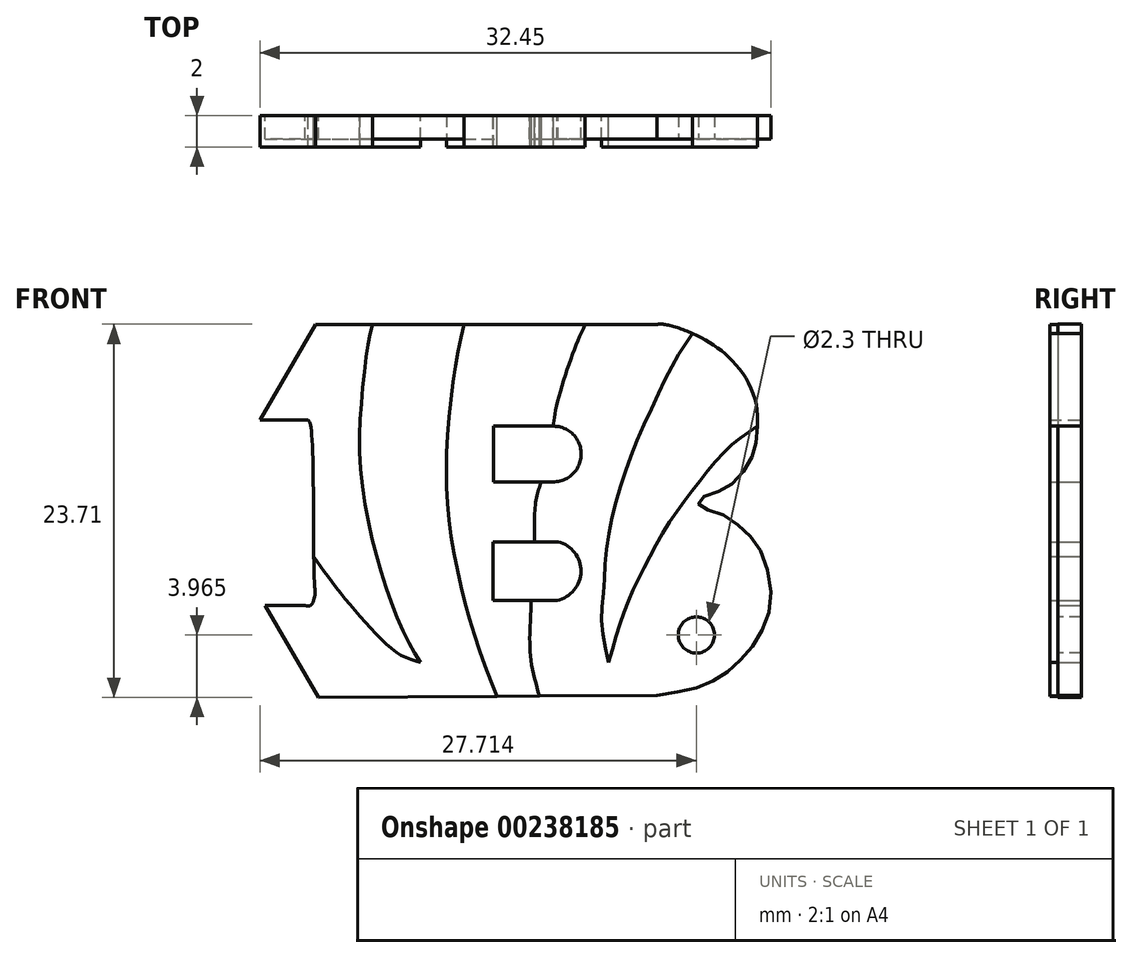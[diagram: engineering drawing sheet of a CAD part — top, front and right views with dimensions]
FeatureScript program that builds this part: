
annotation { "Feature Type Name" : "Feature", "Feature Type Description" : "" }
export const myFeature = defineFeature(function(context is Context, id is Id, definition is map)
    precondition{}
    {
        {
            var Q0;
            Q0=qCreatedBy(makeId("Front.planeOp"),FACE);
            var sketch = newSketch(context, id + "F0", { "sketchPlane" : qUnion([Q0])});
            skLineSegment(sketch, "E0", {"start": v(22.53, 20.5) * mm, "end": v(22.53, 16.97) * mm});
            skLineSegment(sketch, "E1", {"start": v(22.53, 16.97) * mm, "end": v(26.3, 16.97) * mm});
            skLineSegment(sketch, "E2", {"start": v(22.53, 20.5) * mm, "end": v(26.34, 20.5) * mm});
            skArc(sketch, "E3", {"start": v(26.3, 16.97) * mm, "mid": v(28.1, 18.71) * mm, "end": v(26.34, 20.5) * mm});
            skLineSegment(sketch, "E4", {"start": v(22.5, 13.16) * mm, "end": v(22.5, 9.43) * mm});
            skLineSegment(sketch, "E5", {"start": v(22.5, 9.43) * mm, "end": v(26.57, 9.43) * mm});
            skLineSegment(sketch, "E6", {"start": v(22.5, 13.16) * mm, "end": v(26.64, 13.16) * mm});
            skArc(sketch, "E7", {"start": v(26.57, 9.43) * mm, "mid": v(28.1, 11.27) * mm, "end": v(26.64, 13.16) * mm});
            skLineSegment(sketch, "E8", {"start": v(7.71, 20.9) * mm, "end": v(11.24, 26.96) * mm});
            skLineSegment(sketch, "E9", {"start": v(11.24, 26.96) * mm, "end": v(32.9, 26.96) * mm});
            skFitSpline(sketch, "E10", {"points": [v(32.9, 26.96) * mm, v(33.42, 26.96) * mm, v(34.85, 26.53) * mm, v(36.5, 25.65) * mm, v(38.05, 24.27) * mm, v(39.2, 21.97) * mm, v(39.24, 19.75) * mm, v(38.93, 18.48) * mm, v(37.9, 17.02) * mm, v(36.63, 16.27) * mm, v(35.6, 15.83) * mm, v(35.68, 15.4) * mm, v(36.83, 15) * mm, v(38.37, 13.97) * mm, v(39.48, 12.62) * mm, v(40.15, 9.93) * mm, v(39.64, 7.6) * mm, v(38.45, 5.89) * mm, v(37.06, 4.66) * mm, v(35.36, 3.87) * mm, v(32.9, 3.4) * mm], "startDerivative": vector(16.4, 1.57) * mm, "endDerivative": vector(-42.3, -6.3) * mm});
            skLineSegment(sketch, "E11", {"start": v(7.71, 20.9) * mm, "end": v(10.76, 20.9) * mm});
            skLineSegment(sketch, "E12", {"start": v(11.44, 3.27) * mm, "end": v(32.9, 3.4) * mm});
            skLineSegment(sketch, "E13", {"start": v(11.44, 3.27) * mm, "end": v(8.03, 9.1) * mm});
            skLineSegment(sketch, "E14", {"start": v(8.03, 9.1) * mm, "end": v(10.57, 9.11) * mm});
            skFitSpline(sketch, "E15", {"points": [v(10.57, 9.11) * mm, v(10.92, 9.11) * mm, v(11.2, 9.77) * mm, v(11.16, 10.68) * mm, v(10.96, 20.27) * mm, v(10.76, 20.9) * mm], "startDerivative": vector(4, -1.18) * mm, "endDerivative": vector(-1.7, 2.44) * mm});
            skFitSpline(sketch, "E16", {"points": [v(14.84, 26.96) * mm, v(14.53, 25.42) * mm, v(14.17, 22.25) * mm, v(14.05, 18.56) * mm, v(14.65, 14.17) * mm, v(15.71, 10.29) * mm, v(16.94, 7.16) * mm, v(17.9, 5.5) * mm], "startDerivative": vector(-3.2, -13.7) * mm, "endDerivative": vector(8.42, -13.46) * mm});
            skFitSpline(sketch, "E17", {"points": [v(11.12, 12.23) * mm, v(12.43, 10.4) * mm, v(14.49, 7.95) * mm, v(16.5, 6.05) * mm, v(17.9, 5.5) * mm], "startDerivative": vector(5, -7.27) * mm, "endDerivative": vector(6.9, -1.93) * mm});
            skFitSpline(sketch, "E18", {"points": [v(20.67, 26.96) * mm, v(20.07, 24) * mm, v(19.6, 19.44) * mm, v(19.64, 15.2) * mm, v(20.3, 11.08) * mm, v(21.38, 7.04) * mm, v(22.77, 3.34) * mm], "startDerivative": vector(-4.31, -19.23) * mm, "endDerivative": vector(8.83, -22.03) * mm});
            skFitSpline(sketch, "E19", {"points": [v(28.35, 26.96) * mm, v(27.44, 24.74) * mm, v(26.53, 21.7) * mm, v(26.34, 20.5) * mm], "startDerivative": vector(-2.58, -5.82) * mm, "endDerivative": vector(-0.46, -4.18) * mm});
            skFitSpline(sketch, "E20", {"points": [v(25.58, 16.97) * mm, v(25.22, 15.71) * mm, v(25.14, 13.16) * mm], "startDerivative": vector(-1, -2.73) * mm, "endDerivative": vector(0.07, -4.78) * mm});
            skFitSpline(sketch, "E21", {"points": [v(24.94, 9.43) * mm, v(24.86, 7.9) * mm, v(24.9, 5.73) * mm, v(25.46, 3.35) * mm], "startDerivative": vector(-0.29, -5.03) * mm, "endDerivative": vector(1.88, -6.48) * mm});
            skFitSpline(sketch, "E22", {"points": [v(35.18, 26.38) * mm, v(34.1, 24.7) * mm, v(32.87, 22.25) * mm, v(31.4, 18.96) * mm, v(30.4, 15.99) * mm, v(29.74, 12.86) * mm, v(29.54, 10.2) * mm, v(29.42, 7.9) * mm, v(29.86, 5.5) * mm], "startDerivative": vector(-10.35, -14.93) * mm, "endDerivative": vector(4.97, -20.58) * mm});
            skFitSpline(sketch, "E23", {"points": [v(39.3, 20.5) * mm, v(37.54, 19.2) * mm, v(35.6, 16.97) * mm, v(33.7, 14.37) * mm, v(32.03, 11.4) * mm, v(30.85, 8.74) * mm, v(29.86, 5.5) * mm], "startDerivative": vector(-12.54, -8.09) * mm, "endDerivative": vector(-5.25, -18.97) * mm});
            skSolve(sketch);
        }
        {
            var Q0;
            {var subQ4=sQuery(id+"F0.wireOp",EDGE,"E13");Q0=makeQuery(id+"F0.imprint","IMPRINT",FACE,{"disambiguationData":[TD([[makeQuery(id+"F0.imprint","IMPRINT",EDGE,{"derivedFrom":subQ4}),-1.0]])]});}
            var Q1;
            {var subQ10=sQuery(id+"F0.wireOp",EDGE,"E3");Q1=makeQuery(id+"F0.imprint","IMPRINT",FACE,{"disambiguationData":[TD([[makeQuery(id+"F0.imprint","IMPRINT",EDGE,{"derivedFrom":subQ10}),-1.0]])]});}
            extrude(context, id + "F1", {"entities" : qUnion([Q0, Q1]), "depth" : 1.5 * mm});
        }
        {
            var Q0;
            {var subQ2=sQuery(id+"F0.wireOp",EDGE,"E8");Q0=makeQuery(id+"F0.imprint","IMPRINT",FACE,{"disambiguationData":[TD([[makeQuery(id+"F0.imprint","IMPRINT",EDGE,{"derivedFrom":subQ2}),-1.0]])]});}
            var Q1;
            {var subQ8=sQuery(id+"F0.wireOp",EDGE,"E0");Q1=makeQuery(id+"F0.imprint","IMPRINT",FACE,{"disambiguationData":[TD([[makeQuery(id+"F0.imprint","IMPRINT",EDGE,{"derivedFrom":subQ8}),-1.0]])]});}
            var Q2;
            {var subQ0=sQuery(id+"F0.wireOp",EDGE,"E22");Q2=makeQuery(id+"F0.imprint","IMPRINT",FACE,{"disambiguationData":[TD([[makeQuery(id+"F0.imprint","IMPRINT",EDGE,{"derivedFrom":subQ0}),1.0]])]});}
            extrude(context, id + "F2", {"entities" : qUnion([Q0, Q1, Q2]), "depth" : 2 * mm});
        }
        {
            var Q0;
            Q0=makeQuery(id+"F1.opExtrude","CAP_FACE",FACE,{"disambiguationData":[OSD([sQuery(id+"F0.wireOp",EDGE,"E1"),sQuery(id+"F0.wireOp",EDGE,"E3"),sQuery(id+"F0.wireOp",EDGE,"E5"),sQuery(id+"F0.wireOp",EDGE,"E6"),sQuery(id+"F0.wireOp",EDGE,"E7"),sQuery(id+"F0.wireOp",EDGE,"E9"),sQuery(id+"F0.wireOp",EDGE,"E10"),sQuery(id+"F0.wireOp",EDGE,"E12"),sQuery(id+"F0.wireOp",EDGE,"E19"),sQuery(id+"F0.wireOp",EDGE,"E20"),sQuery(id+"F0.wireOp",EDGE,"E21"),sQuery(id+"F0.wireOp",EDGE,"E22"),sQuery(id+"F0.wireOp",EDGE,"E23")])],"isStart":false});
            var sketch = newSketch(context, id + "F3", { "sketchPlane" : qUnion([Q0])});
            skCircle(sketch, "E24", {"center": v(35.42, 7.24) * mm, "radius": 1.15 * mm});
            skSolve(sketch);
        }
        {
            var Q0;
            Q0 = qSketchRegion(id + "F3", true);
            extrude(context, id + "F4", {"entities" : qUnion([Q0]), "operationType" : NewBodyOperationType.REMOVE, "oppositeDirection" : true, "depth" : 25 * mm});
        }
    });
